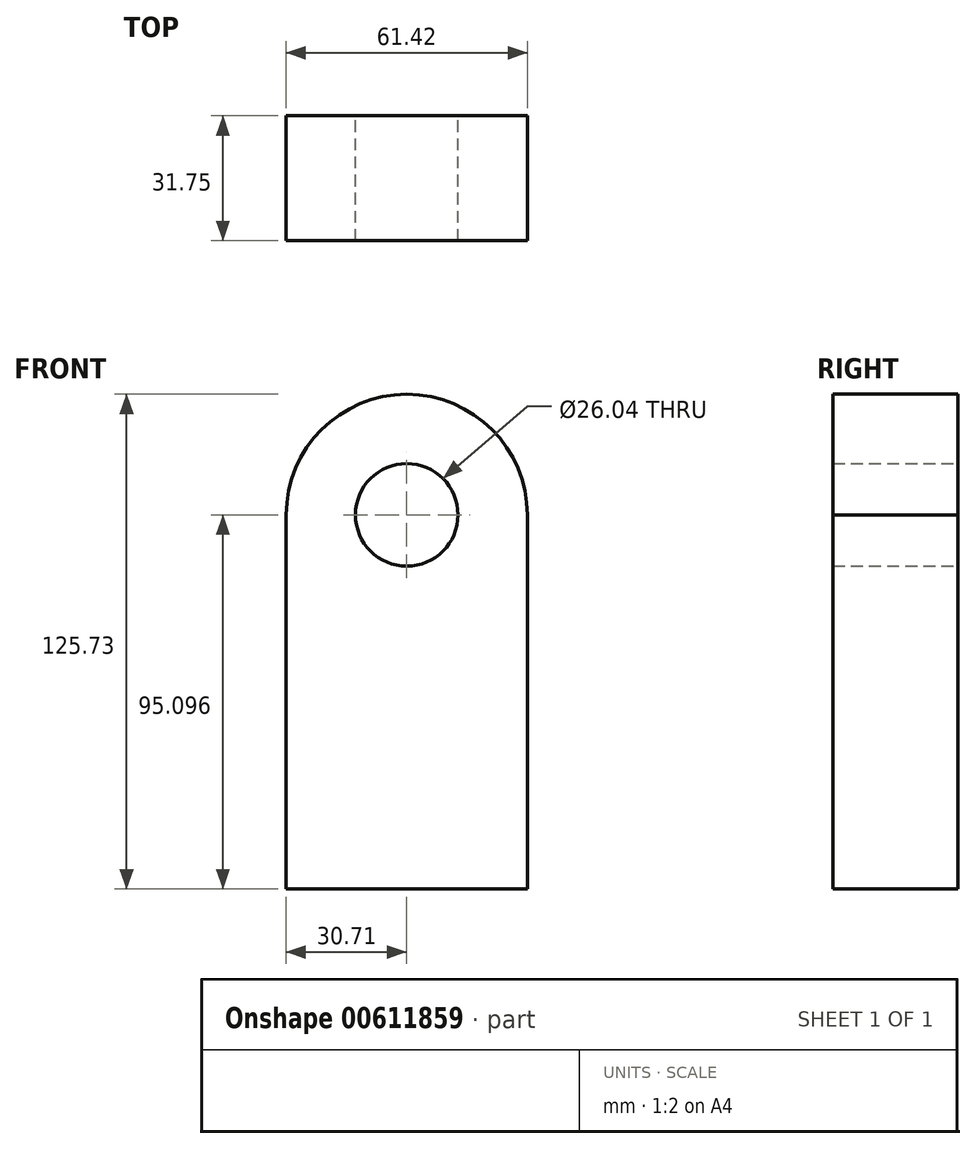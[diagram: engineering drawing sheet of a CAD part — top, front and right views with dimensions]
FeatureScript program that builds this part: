
annotation { "Feature Type Name" : "Feature", "Feature Type Description" : "" }
export const myFeature = defineFeature(function(context is Context, id is Id, definition is map)
    precondition{}
    {
        {
            var Q0;
            Q0=qCreatedBy(makeId("Front.planeOp"),FACE);
            var sketch = newSketch(context, id + "F0", { "sketchPlane" : qUnion([Q0])});
            skLineSegment(sketch, "E0.bottom", {"start": v(30.7, -47.55) * mm, "end": v(-30.7, -47.55) * mm});
            skLineSegment(sketch, "E0.top", {"start": v(30.7, 47.55) * mm, "end": v(-30.7, 47.55) * mm});
            skLineSegment(sketch, "E0.left", {"start": v(30.7, -47.55) * mm, "end": v(30.7, 47.55) * mm});
            skLineSegment(sketch, "E0.right", {"start": v(-30.7, -47.55) * mm, "end": v(-30.7, 47.55) * mm});
            skPoint(sketch, "E0.middle", {"position": v(0, 0) * mm});
            skArc(sketch, "E1", {"start": v(30.63, 47.55) * mm, "mid": v(0, 78.18) * mm, "end": v(-30.63, 47.55) * mm});
            skCircle(sketch, "E2", {"center": v(0, 47.55) * mm, "radius": 13.02 * mm});
            skArc(sketch, "E3", {"start": v(-30.7, 47.55) * mm, "mid": v(0, 78.25) * mm, "end": v(30.7, 47.55) * mm});
            skPoint(sketch, "E4.start.orphan", {"position": v(0, 16.92) * mm});
            skSolve(sketch);
        }
        {
            var Q0;
            Q0=makeQuery(id+"F0.imprint","IMPRINT",FACE,{"disambiguationData":[TD([[makeQuery(id+"F0.imprint","IMPRINT",EDGE,{"derivedFrom":sQuery(id+"F0.wireOp",EDGE,"E0.bottom")}),-1.0]])]});
            var Q1;
            {var subQ0=sQuery(id+"F0.wireOp",EDGE,"E1");Q1=makeQuery(id+"F0.imprint","IMPRINT",FACE,{"disambiguationData":[TD([[makeQuery(id+"F0.imprint","IMPRINT",EDGE,{"derivedFrom":subQ0}),1.0]])]});}
            extrude(context, id + "F1", {"entities" : qUnion([Q0, Q1]), "depth" : 31.75 * mm, "offsetDistance" : 25.4 * mm});
        }
    });
